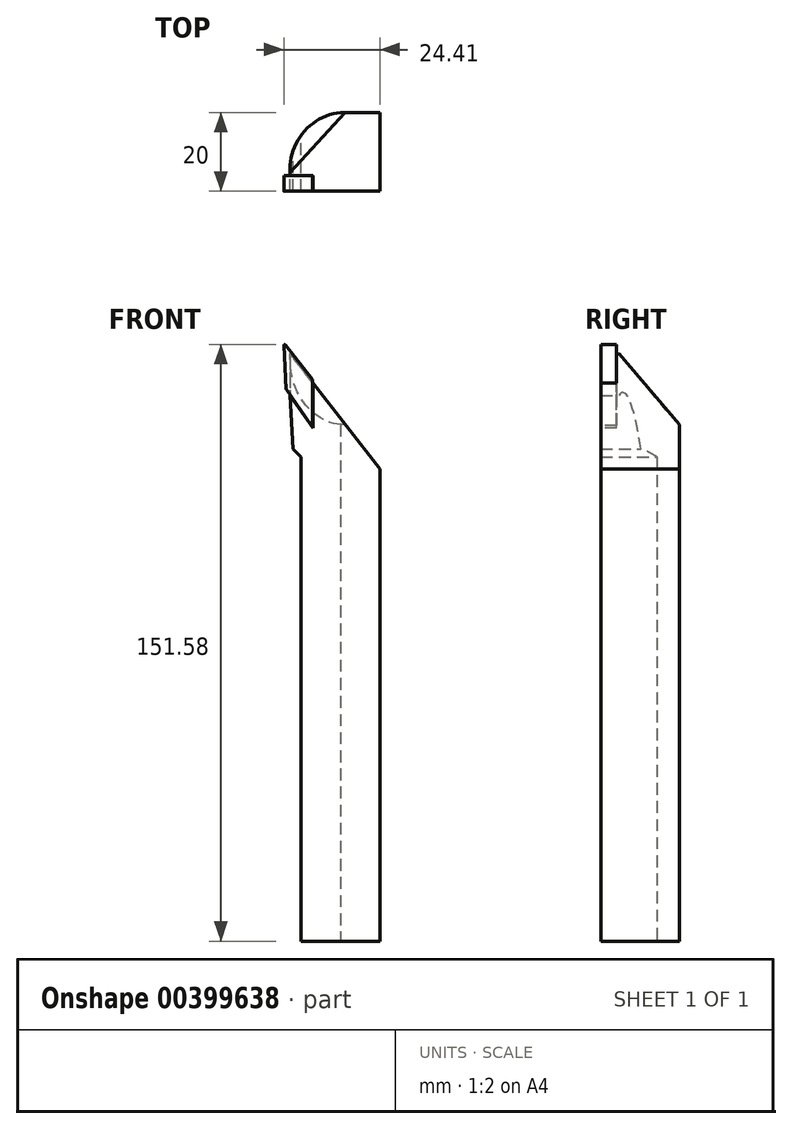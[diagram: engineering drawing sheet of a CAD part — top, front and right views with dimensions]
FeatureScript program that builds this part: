
annotation { "Feature Type Name" : "Feature", "Feature Type Description" : "" }
export const myFeature = defineFeature(function(context is Context, id is Id, definition is map)
    precondition{}
    {
        {
            var Q0;
            Q0=qCreatedBy(makeId("Front.planeOp"),FACE);
            var sketch = newSketch(context, id + "F0", { "sketchPlane" : qUnion([Q0])});
            skLineSegment(sketch, "E0", {"start": v(0, 0) * mm, "end": v(20, 0) * mm});
            skLineSegment(sketch, "E1", {"start": v(20, 0) * mm, "end": v(20, 120) * mm});
            skLineSegment(sketch, "E2", {"start": v(20, 120) * mm, "end": v(-3.44, 150) * mm});
            skLineSegment(sketch, "E3", {"start": v(-2.13, 125) * mm, "end": v(0, 123) * mm});
            skLineSegment(sketch, "E4", {"start": v(0, 123) * mm, "end": v(0, 0) * mm});
            skLineSegment(sketch, "E5", {"start": v(-3.44, 150) * mm, "end": v(-2.13, 125) * mm});
            skSolve(sketch);
        }
        {
            var Q0;
            Q0=makeQuery(id+"F0.imprint","IMPRINT",FACE,{"disambiguationData":[TD([[makeQuery(id+"F0.imprint","IMPRINT",EDGE,{"derivedFrom":sQuery(id+"F0.wireOp",EDGE,"E0")}),1.0]])]});
            extrude(context, id + "F1", {"entities" : qUnion([Q0]), "depth" : 20 * mm});
        }
        {
            var Q0;
            Q0=makeQuery(id+"F1.opExtrude","CAP_FACE",FACE,{"disambiguationData":[OSD([sQuery(id+"F0.wireOp",EDGE,"E0"),sQuery(id+"F0.wireOp",EDGE,"E1"),sQuery(id+"F0.wireOp",EDGE,"E2"),sQuery(id+"F0.wireOp",EDGE,"E3"),sQuery(id+"F0.wireOp",EDGE,"E4"),sQuery(id+"F0.wireOp",EDGE,"E5")])],"isStart":false});
            var sketch = newSketch(context, id + "F2", { "sketchPlane" : qUnion([Q0])});
            skLineSegment(sketch, "E6", {"start": v(-4.44, 152) * mm, "end": v(-3.8, 140) * mm});
            skLineSegment(sketch, "E7", {"start": v(-3.8, 140) * mm, "end": v(2.95, 130.35) * mm});
            skLineSegment(sketch, "E8", {"start": v(2.95, 130.35) * mm, "end": v(2.95, 142.54) * mm});
            skLineSegment(sketch, "E9", {"start": v(2.95, 142.54) * mm, "end": v(-4.44, 152) * mm});
            skLineSegment(sketch, "E10.0", {"start": v(3.05, 130.03) * mm, "end": v(3.05, 142.54) * mm});
            skLineSegment(sketch, "E10.1", {"start": v(-3.9, 139.94) * mm, "end": v(3.05, 130.03) * mm});
            skLineSegment(sketch, "E11", {"start": v(3.05, 142.54) * mm, "end": v(2.95, 142.54) * mm});
            skLineSegment(sketch, "E12", {"start": v(-3.9, 139.94) * mm, "end": v(-3.8, 140) * mm});
            skSolve(sketch);
        }
        {
            var Q0;
            {var subQ5=sQuery(id+"F2.wireOp",EDGE,"E6");Q0=makeQuery(id+"F2.imprint","IMPRINT",FACE,{"disambiguationData":[TD([[makeQuery(id+"F2.imprint","IMPRINT",EDGE,{"derivedFrom":subQ5}),1.0]])]});}
            var Q1;
            {var subQ0=sQuery(id+"F2.wireOp",EDGE,"E8");var subQ1=sQuery(id+"F2.wireOp",EDGE,"E7");var subQ2=makeQuery(id+"F2.imprint","INTERSECT",VERTEX,{"derivedFrom":[subQ1,subQ0]});Q1=makeQuery(id+"F2.imprint","IMPRINT",FACE,{"disambiguationData":[TD([[makeQuery(id+"F2.imprint","IMPRINT",EDGE,{"disambiguationData":[TD([[subQ2,1.0]])],"derivedFrom":subQ1}),1.0]])]});}
            extrude(context, id + "F3", {"entities" : qUnion([Q0, Q1]), "operationType" : NewBodyOperationType.ADD, "depth" : 0 * mm, "hasSecondDirection" : true, "secondDirectionOppositeDirection" : true, "secondDirectionDepth" : 4 * mm});
        }
        {
            var Q0;
            Q0=makeQuery(id+"F3.boolean.opBoolean","MERGE",FACE,{"derivedFrom":[makeQuery(id+"F1.opExtrude","CAP_FACE",FACE,{"disambiguationData":[OSD([sQuery(id+"F0.wireOp",EDGE,"E0"),sQuery(id+"F0.wireOp",EDGE,"E1"),sQuery(id+"F0.wireOp",EDGE,"E2"),sQuery(id+"F0.wireOp",EDGE,"E3"),sQuery(id+"F0.wireOp",EDGE,"E4"),sQuery(id+"F0.wireOp",EDGE,"E5")])],"isStart":false}),makeQuery(id+"F3.opExtrude","CAP_FACE",FACE,{"disambiguationData":[OSD([sQuery(id+"F2.wireOp",EDGE,"E6"),sQuery(id+"F2.wireOp",EDGE,"E7"),sQuery(id+"F2.wireOp",EDGE,"E8"),sQuery(id+"F2.wireOp",EDGE,"E9")])],"isStart":false})]});
            var sketch = newSketch(context, id + "F4", { "sketchPlane" : qUnion([Q0])});
            skLineSegment(sketch, "E13.0", {"start": v(2.95, 130.34) * mm, "end": v(2.95, 142.85) * mm});
            skLineSegment(sketch, "E13.1", {"start": v(-4, 140.25) * mm, "end": v(2.95, 130.34) * mm});
            skLineSegment(sketch, "E14", {"start": v(2.95, 142.85) * mm, "end": v(2.85, 142.85) * mm});
            skLineSegment(sketch, "E15", {"start": v(-4, 140.25) * mm, "end": v(-3.9, 140.3) * mm});
            skLineSegment(sketch, "E16", {"start": v(-3.9, 140.3) * mm, "end": v(2.88, 130.62) * mm});
            skLineSegment(sketch, "E17", {"start": v(2.88, 130.62) * mm, "end": v(2.85, 142.85) * mm});
            skSolve(sketch);
        }
        {
            var Q0;
            Q0 = qSketchRegion(id + "F4", true);
            extrude(context, id + "F5", {"entities" : qUnion([Q0]), "operationType" : NewBodyOperationType.REMOVE, "oppositeDirection" : true, "depth" : 4 * mm});
        }
        {
            var Q0;
            Q0=makeQuery(id+"F3.opExtrude","SWEPT_EDGE",EDGE,{"disambiguationData":[OSD([sQuery(id+"F2.wireOp",EDGE,"E6"),sQuery(id+"F2.wireOp",EDGE,"E9")])]});
            var Q1;
            Q1=makeQuery(id+"F5.boolean.opBoolean","COPY",EDGE,{"derivedFrom":makeQuery(id+"F5.opExtrude","SWEPT_EDGE",EDGE,{"disambiguationData":[OSD([sQuery(id+"F4.wireOp",EDGE,"E16"),sQuery(id+"F4.wireOp",EDGE,"E17")])]})});
            var Q2;
            Q2=makeQuery(id+"F5.boolean.opBoolean","INTERSECT",EDGE,{"derivedFrom":[makeQuery(id+"F3.opExtrude","SWEPT_FACE",FACE,{"disambiguationData":[OSD([sQuery(id+"F2.wireOp",EDGE,"E6")])]}),makeQuery(id+"F5.opExtrude","SWEPT_FACE",FACE,{"disambiguationData":[OSD([sQuery(id+"F4.wireOp",EDGE,"E16")])]})]});
            var Q3;
            Q3=makeQuery(id+"F5.boolean.opBoolean","INTERSECT",EDGE,{"derivedFrom":[makeQuery(id+"F3.opExtrude","SWEPT_FACE",FACE,{"disambiguationData":[OSD([sQuery(id+"F2.wireOp",EDGE,"E9")])]}),makeQuery(id+"F5.opExtrude","SWEPT_FACE",FACE,{"disambiguationData":[OSD([sQuery(id+"F4.wireOp",EDGE,"E17")])]})]});
            fillet(context, id + "F6", {"entities" : qUnion([Q0, Q1, Q2, Q3]), "radius" : 0.2 * mm, "tangentPropagation" : true, "allowEdgeOverflow" : false});
        }
        {
            var Q0;
            Q0=makeQuery(id+"F1.opExtrude","SWEPT_FACE",FACE,{"disambiguationData":[OSD([sQuery(id+"F0.wireOp",EDGE,"E5")])]});
            var sketch = newSketch(context, id + "F7", { "sketchPlane" : qUnion([Q0])});
            skLineSegment(sketch, "E18", {"start": v(16, 149.97) * mm, "end": v(0, 130.57) * mm});
            skLineSegment(sketch, "E19", {"start": v(0, 130.57) * mm, "end": v(-5.45, 130.57) * mm});
            skLineSegment(sketch, "E20", {"start": v(-5.45, 130.57) * mm, "end": v(-5.45, 152.34) * mm});
            skLineSegment(sketch, "E21", {"start": v(-5.45, 152.34) * mm, "end": v(16, 152.34) * mm});
            skLineSegment(sketch, "E22", {"start": v(16, 152.34) * mm, "end": v(16, 149.97) * mm});
            skSolve(sketch);
        }
        {
            var Q0;
            {var subQ0=sQuery(id+"F7.wireOp",EDGE,"E18");Q0=makeQuery(id+"F7.imprint","IMPRINT",FACE,{"disambiguationData":[TD([[makeQuery(id+"F7.imprint","IMPRINT",EDGE,{"derivedFrom":subQ0}),-1.0]])]});}
            var Q1;
            {var subQ0=sQuery(id+"F7.wireOp",EDGE,"E19");Q1=makeQuery(id+"F7.imprint","IMPRINT",FACE,{"disambiguationData":[TD([[makeQuery(id+"F7.imprint","IMPRINT",EDGE,{"derivedFrom":subQ0}),-1.0]])]});}
            extrude(context, id + "F8", {"entities" : qUnion([Q0, Q1]), "operationType" : NewBodyOperationType.REMOVE, "oppositeDirection" : true, "depth" : 25 * mm, "hasSecondDirection" : true, "secondDirectionOppositeDirection" : false, "secondDirectionDepth" : 25 * mm});
        }
        {
            var Q0;
            Q0=qCreatedBy(makeId("Top.planeOp"),FACE);
            var sketch = newSketch(context, id + "F9", { "sketchPlane" : qUnion([Q0])});
            skArc(sketch, "E23", {"start": v(10.86, 0.07) * mm, "mid": v(0.57, -5.02) * mm, "end": v(-2.8, -16) * mm});
            skArc(sketch, "E24", {"start": v(10.86, 10.58) * mm, "mid": v(-6.87, 2.42) * mm, "end": v(-13.33, -16) * mm});
            skLineSegment(sketch, "E25", {"start": v(-2.8, -16) * mm, "end": v(-13.33, -16) * mm});
            skLineSegment(sketch, "E26", {"start": v(10.86, 10.58) * mm, "end": v(10.86, 0.07) * mm});
            skSolve(sketch);
        }
        {
            var Q0;
            Q0 = qSketchRegion(id + "F9", true);
            extrude(context, id + "F10", {"entities" : qUnion([Q0]), "operationType" : NewBodyOperationType.REMOVE, "depth" : 150 * mm});
        }
    });
